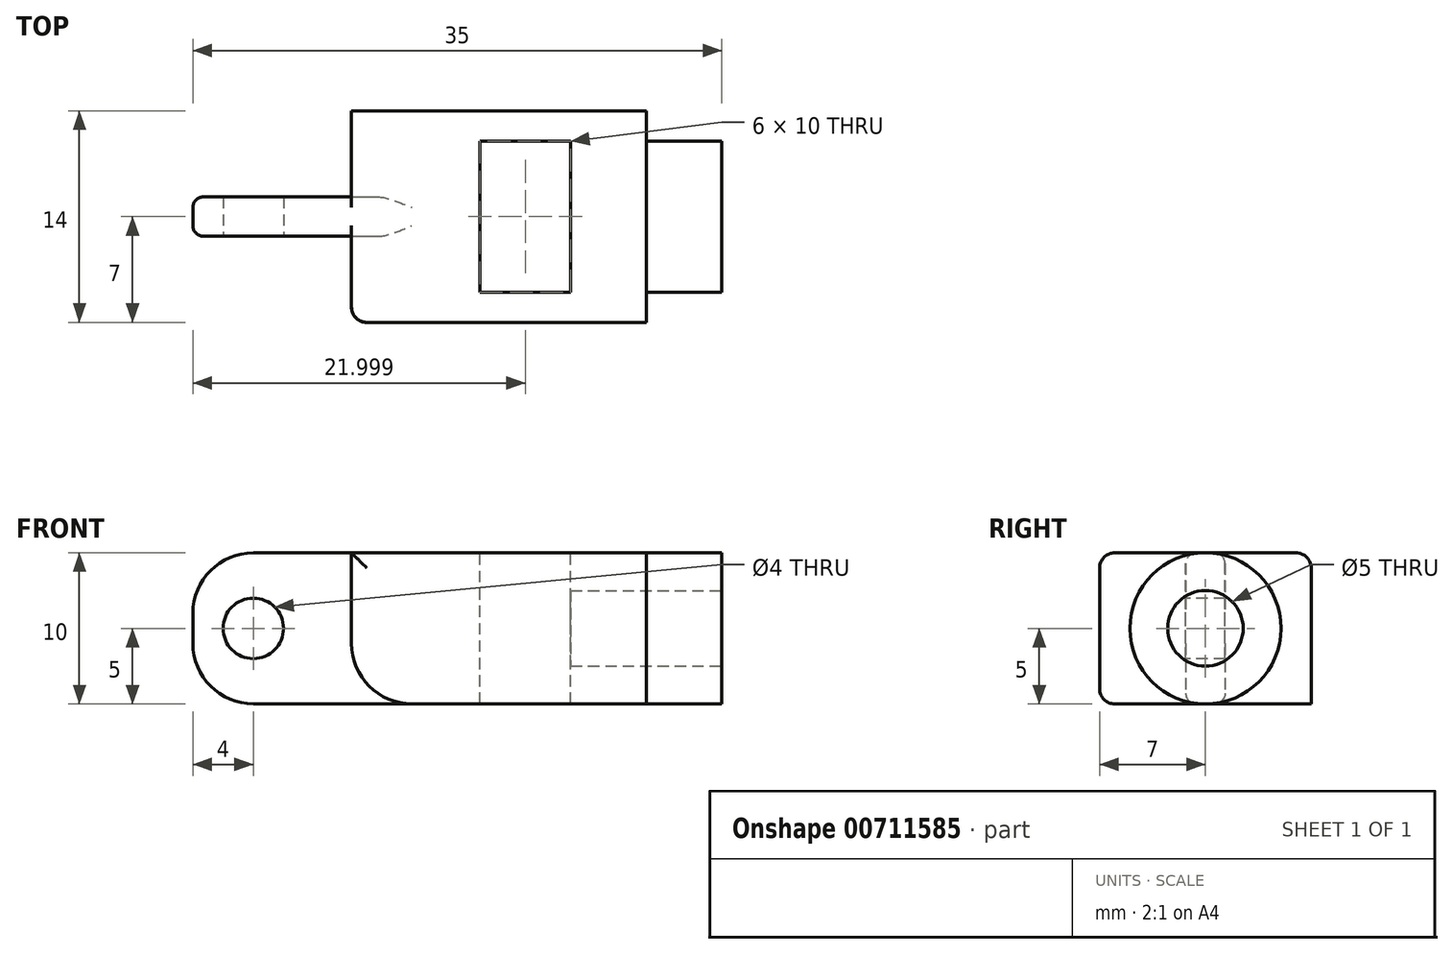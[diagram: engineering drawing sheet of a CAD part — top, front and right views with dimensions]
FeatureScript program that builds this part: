
annotation { "Feature Type Name" : "Feature", "Feature Type Description" : "" }
export const myFeature = defineFeature(function(context is Context, id is Id, definition is map)
    precondition{}
    {
        {
            var Q0;
            Q0=qCreatedBy(makeId("Top.planeOp"),FACE);
            var sketch = newSketch(context, id + "F0", { "sketchPlane" : qUnion([Q0])});
            skLineSegment(sketch, "E0.bottom", {"start": v(-15, 7) * mm, "end": v(15, 7) * mm});
            skLineSegment(sketch, "E0.top", {"start": v(-15, -7) * mm, "end": v(15, -7) * mm});
            skLineSegment(sketch, "E0.left", {"start": v(-15, 7) * mm, "end": v(-15, -7) * mm});
            skLineSegment(sketch, "E0.right", {"start": v(15, 7) * mm, "end": v(15, -7) * mm});
            skLineSegment(sketch, "E1", {"start": v(-15, 0) * mm, "end": v(0, 0) * mm, "construction": true});
            skLineSegment(sketch, "E2", {"start": v(0, 7) * mm, "end": v(0, -0.57) * mm, "construction": true});
            skSolve(sketch);
        }
        {
            var Q0;
            Q0=makeQuery(id+"F0.imprint","IMPRINT",FACE,{"disambiguationData":[TD([[makeQuery(id+"F0.imprint","IMPRINT",EDGE,{"derivedFrom":sQuery(id+"F0.wireOp",EDGE,"E0.bottom")}),-1.0]])]});
            extrude(context, id + "F1", {"entities" : qUnion([Q0]), "depth" : 10 * mm, "offsetDistance" : 25 * mm});
        }
        {
            var Q0;
            Q0=makeQuery(id+"F1.opExtrude","CAP_FACE",FACE,{"disambiguationData":[OSD([sQuery(id+"F0.wireOp",EDGE,"E0.bottom"),sQuery(id+"F0.wireOp",EDGE,"E0.top"),sQuery(id+"F0.wireOp",EDGE,"E0.left"),sQuery(id+"F0.wireOp",EDGE,"E0.right")])],"isStart":false});
            var sketch = newSketch(context, id + "F2", { "sketchPlane" : qUnion([Q0])});
            skLineSegment(sketch, "E3.bottom", {"start": v(-15, -1.3) * mm, "end": v(-4.5, -1.3) * mm});
            skLineSegment(sketch, "E3.top", {"start": v(-15, -7) * mm, "end": v(-4.5, -7) * mm});
            skLineSegment(sketch, "E3.left", {"start": v(-15, -1.3) * mm, "end": v(-15, -7) * mm});
            skLineSegment(sketch, "E3.right", {"start": v(-4.5, -1.3) * mm, "end": v(-4.5, -7) * mm});
            skPoint(sketch, "E4.oppositeSnap0", {"position": v(-4.5, -4.15) * mm});
            skLineSegment(sketch, "E4.bottom", {"start": v(-15, 7) * mm, "end": v(-4.5, 7) * mm});
            skLineSegment(sketch, "E4.top", {"start": v(-15, 1.3) * mm, "end": v(-4.5, 1.3) * mm});
            skLineSegment(sketch, "E4.left", {"start": v(-15, 7) * mm, "end": v(-15, 1.3) * mm});
            skLineSegment(sketch, "E4.right", {"start": v(-4.5, 7) * mm, "end": v(-4.5, 1.3) * mm});
            skSolve(sketch);
        }
        {
            var Q0;
            Q0=makeQuery(id+"F2.imprint","IMPRINT",FACE,{"disambiguationData":[TD([[makeQuery(id+"F2.imprint","IMPRINT",EDGE,{"derivedFrom":sQuery(id+"F2.wireOp",EDGE,"E3.bottom")}),-1.0]])]});
            var Q1;
            Q1=makeQuery(id+"F2.imprint","IMPRINT",FACE,{"disambiguationData":[TD([[makeQuery(id+"F2.imprint","IMPRINT",EDGE,{"derivedFrom":sQuery(id+"F2.wireOp",EDGE,"E4.bottom")}),-1.0]])]});
            extrude(context, id + "F3", {"entities" : qUnion([Q0, Q1]), "operationType" : NewBodyOperationType.REMOVE, "oppositeDirection" : true, "depth" : 25 * mm, "offsetDistance" : 25 * mm});
        }
        {
            var Q0;
            Q0=makeQuery(id+"F1.opExtrude","CAP_EDGE",EDGE,{"disambiguationData":[OSD([sQuery(id+"F0.wireOp",EDGE,"E0.left")])],"isStart":false});
            var Q1;
            Q1=makeQuery(id+"F1.opExtrude","CAP_EDGE",EDGE,{"disambiguationData":[OSD([sQuery(id+"F0.wireOp",EDGE,"E0.left")])],"isStart":true});
            var Q2;
            Q2=makeQuery(id+"F3.boolean.opBoolean","COPY",EDGE,{"derivedFrom":makeQuery(id+"F3.opExtrude","CAP_EDGE",EDGE,{"disambiguationData":[OSD([sQuery(id+"F2.wireOp",EDGE,"E3.right")])],"isStart":true})});
            var Q3;
            Q3=makeQuery(id+"F3.boolean.opBoolean","INTERSECT",EDGE,{"derivedFrom":[makeQuery(id+"F1.opExtrude","CAP_FACE",FACE,{"disambiguationData":[OSD([sQuery(id+"F0.wireOp",EDGE,"E0.bottom"),sQuery(id+"F0.wireOp",EDGE,"E0.top"),sQuery(id+"F0.wireOp",EDGE,"E0.left"),sQuery(id+"F0.wireOp",EDGE,"E0.right")])],"isStart":true}),makeQuery(id+"F3.opExtrude","SWEPT_FACE",FACE,{"disambiguationData":[OSD([sQuery(id+"F2.wireOp",EDGE,"E3.right")])]})]});
            var Q4;
            Q4=makeQuery(id+"F3.boolean.opBoolean","INTERSECT",EDGE,{"derivedFrom":[makeQuery(id+"F1.opExtrude","CAP_FACE",FACE,{"disambiguationData":[OSD([sQuery(id+"F0.wireOp",EDGE,"E0.bottom"),sQuery(id+"F0.wireOp",EDGE,"E0.top"),sQuery(id+"F0.wireOp",EDGE,"E0.left"),sQuery(id+"F0.wireOp",EDGE,"E0.right")])],"isStart":true}),makeQuery(id+"F3.opExtrude","SWEPT_FACE",FACE,{"disambiguationData":[OSD([sQuery(id+"F2.wireOp",EDGE,"E4.right")])]})]});
            var Q5;
            Q5=makeQuery(id+"F3.boolean.opBoolean","COPY",EDGE,{"derivedFrom":makeQuery(id+"F3.opExtrude","CAP_EDGE",EDGE,{"disambiguationData":[OSD([sQuery(id+"F2.wireOp",EDGE,"E4.right")])],"isStart":true})});
            fillet(context, id + "F4", {"entities" : qUnion([Q0, Q1, Q2, Q3, Q4, Q5]), "radius" : 4 * mm, "tangentPropagation" : true, "allowEdgeOverflow" : false});
        }
        {
            var Q0;
            Q0=makeQuery(id+"F3.boolean.opBoolean","COPY",FACE,{"derivedFrom":makeQuery(id+"F3.opExtrude","SWEPT_FACE",FACE,{"disambiguationData":[OSD([sQuery(id+"F2.wireOp",EDGE,"E3.bottom")])]})});
            var sketch = newSketch(context, id + "F5", { "sketchPlane" : qUnion([Q0])});
            skCircle(sketch, "E5", {"center": v(-11, 5) * mm, "radius": 2 * mm});
            skPoint(sketch, "E5.centerSnap0", {"position": v(-15, 5) * mm});
            skSolve(sketch);
        }
        {
            var Q0;
            Q0=makeQuery(id+"F5.imprint","IMPRINT",FACE,{"disambiguationData":[TD([[makeQuery(id+"F5.imprint","IMPRINT",EDGE,{"derivedFrom":sQuery(id+"F5.wireOp",EDGE,"E5")}),1.0]])]});
            extrude(context, id + "F6", {"entities" : qUnion([Q0]), "operationType" : NewBodyOperationType.REMOVE, "oppositeDirection" : true, "depth" : 25 * mm, "offsetDistance" : 25 * mm});
        }
        {
            var Q0;
            Q0=makeQuery(id+"F1.opExtrude","SWEPT_FACE",FACE,{"disambiguationData":[OSD([sQuery(id+"F0.wireOp",EDGE,"E0.right")])]});
            var sketch = newSketch(context, id + "F7", { "sketchPlane" : qUnion([Q0])});
            skPoint(sketch, "E6.oppositeSnap0", {"position": v(7, 5) * mm});
            skPoint(sketch, "E7.centerSnap0", {"position": v(0, 10) * mm});
            skCircle(sketch, "E8", {"center": v(0, 5) * mm, "radius": 5 * mm});
            skSolve(sketch);
        }
        {
            var Q0;
            {var subQ0=sQuery(id+"F7.wireOp",EDGE,"E8");var subQ1=sQuery(id+"F0.wireOp",EDGE,"E0.right");var subQ2=makeQuery(id+"F7.imprint","INTERSECT",VERTEX,{"derivedFrom":[makeQuery(id+"F1.opExtrude","CAP_EDGE",EDGE,{"disambiguationData":[OSD([subQ1])],"isStart":false}),subQ0]});Q0=makeQuery(id+"F7.imprint","IMPRINT",FACE,{"disambiguationData":[TD([[makeQuery(id+"F7.imprint","IMPRINT",EDGE,{"disambiguationData":[TD([[subQ2,1.0]])],"derivedFrom":subQ0}),1.0]])]});}
            extrude(context, id + "F8", {"entities" : qUnion([Q0]), "operationType" : NewBodyOperationType.ADD, "depth" : 5 * mm, "offsetDistance" : 25 * mm});
        }
        {
            var Q0;
            Q0=makeQuery(id+"F1.opExtrude","CAP_FACE",FACE,{"disambiguationData":[OSD([sQuery(id+"F0.wireOp",EDGE,"E0.bottom"),sQuery(id+"F0.wireOp",EDGE,"E0.top"),sQuery(id+"F0.wireOp",EDGE,"E0.left"),sQuery(id+"F0.wireOp",EDGE,"E0.right")])],"isStart":false});
            var sketch = newSketch(context, id + "F9", { "sketchPlane" : qUnion([Q0])});
            skLineSegment(sketch, "E9.bottom", {"start": v(10, 5) * mm, "end": v(4, 5) * mm});
            skLineSegment(sketch, "E9.top", {"start": v(10, -5) * mm, "end": v(4, -5) * mm});
            skLineSegment(sketch, "E9.left", {"start": v(10, 5) * mm, "end": v(10, -5) * mm});
            skLineSegment(sketch, "E9.right", {"start": v(4, 5) * mm, "end": v(4, -5) * mm});
            skSolve(sketch);
        }
        {
            var Q0;
            Q0=makeQuery(id+"F9.imprint","IMPRINT",FACE,{"disambiguationData":[TD([[makeQuery(id+"F9.imprint","IMPRINT",EDGE,{"derivedFrom":sQuery(id+"F9.wireOp",EDGE,"E9.bottom")}),1.0]])]});
            extrude(context, id + "F10", {"entities" : qUnion([Q0]), "operationType" : NewBodyOperationType.REMOVE, "oppositeDirection" : true, "depth" : 12 * mm, "offsetDistance" : 25 * mm});
        }
        {
            var Q0;
            Q0=makeQuery(id+"F3.boolean.opBoolean","COPY",EDGE,{"derivedFrom":makeQuery(id+"F3.opExtrude","CAP_EDGE",EDGE,{"disambiguationData":[OSD([sQuery(id+"F2.wireOp",EDGE,"E3.bottom")])],"isStart":true})});
            var Q1;
            Q1=makeQuery(id+"F3.boolean.opBoolean","INTERSECT",EDGE,{"derivedFrom":[makeQuery(id+"F1.opExtrude","CAP_FACE",FACE,{"disambiguationData":[OSD([sQuery(id+"F0.wireOp",EDGE,"E0.bottom"),sQuery(id+"F0.wireOp",EDGE,"E0.top"),sQuery(id+"F0.wireOp",EDGE,"E0.left"),sQuery(id+"F0.wireOp",EDGE,"E0.right")])],"isStart":true}),makeQuery(id+"F3.opExtrude","SWEPT_FACE",FACE,{"disambiguationData":[OSD([sQuery(id+"F2.wireOp",EDGE,"E3.bottom")])]})]});
            var Q2;
            Q2=makeQuery(id+"F4.opFillet","BLEND_EDGE",EDGE,{"blendedFrom":[makeQuery(id+"F1.opExtrude","CAP_EDGE",EDGE,{"disambiguationData":[OSD([sQuery(id+"F0.wireOp",EDGE,"E0.left")])],"isStart":true}),makeQuery(id+"F3.boolean.opBoolean","COPY",FACE,{"derivedFrom":makeQuery(id+"F3.opExtrude","SWEPT_FACE",FACE,{"disambiguationData":[OSD([sQuery(id+"F2.wireOp",EDGE,"E3.bottom")])]})})],"blendedInto":[makeQuery(id+"F3.boolean.opBoolean","COPY",FACE,{"derivedFrom":makeQuery(id+"F3.opExtrude","SWEPT_FACE",FACE,{"disambiguationData":[OSD([sQuery(id+"F2.wireOp",EDGE,"E3.bottom")])]})})]});
            var Q3;
            Q3=makeQuery(id+"F3.boolean.opBoolean","COPY",EDGE,{"derivedFrom":makeQuery(id+"F3.opExtrude","SWEPT_EDGE",EDGE,{"disambiguationData":[OSD([sQuery(id+"F0.wireOp",EDGE,"E0.left"),sQuery(id+"F2.wireOp",EDGE,"E3.bottom"),sQuery(id+"F2.wireOp",EDGE,"E3.left")])]})});
            var Q4;
            Q4=makeQuery(id+"F4.opFillet","BLEND_EDGE",EDGE,{"blendedFrom":[makeQuery(id+"F1.opExtrude","CAP_EDGE",EDGE,{"disambiguationData":[OSD([sQuery(id+"F0.wireOp",EDGE,"E0.left")])],"isStart":false}),makeQuery(id+"F3.boolean.opBoolean","COPY",FACE,{"derivedFrom":makeQuery(id+"F3.opExtrude","SWEPT_FACE",FACE,{"disambiguationData":[OSD([sQuery(id+"F2.wireOp",EDGE,"E3.bottom")])]})})],"blendedInto":[makeQuery(id+"F3.boolean.opBoolean","COPY",FACE,{"derivedFrom":makeQuery(id+"F3.opExtrude","SWEPT_FACE",FACE,{"disambiguationData":[OSD([sQuery(id+"F2.wireOp",EDGE,"E3.bottom")])]})})]});
            var Q5;
            Q5=makeQuery(id+"F3.boolean.opBoolean","INTERSECT",EDGE,{"derivedFrom":[makeQuery(id+"F1.opExtrude","CAP_FACE",FACE,{"disambiguationData":[OSD([sQuery(id+"F0.wireOp",EDGE,"E0.bottom"),sQuery(id+"F0.wireOp",EDGE,"E0.top"),sQuery(id+"F0.wireOp",EDGE,"E0.left"),sQuery(id+"F0.wireOp",EDGE,"E0.right")])],"isStart":true}),makeQuery(id+"F3.opExtrude","SWEPT_FACE",FACE,{"disambiguationData":[OSD([sQuery(id+"F2.wireOp",EDGE,"E4.top")])]})]});
            var Q6;
            Q6=makeQuery(id+"F4.opFillet","BLEND_EDGE",EDGE,{"blendedFrom":[makeQuery(id+"F1.opExtrude","CAP_EDGE",EDGE,{"disambiguationData":[OSD([sQuery(id+"F0.wireOp",EDGE,"E0.left")])],"isStart":true}),makeQuery(id+"F3.boolean.opBoolean","COPY",FACE,{"derivedFrom":makeQuery(id+"F3.opExtrude","SWEPT_FACE",FACE,{"disambiguationData":[OSD([sQuery(id+"F2.wireOp",EDGE,"E4.top")])]})})],"blendedInto":[makeQuery(id+"F3.boolean.opBoolean","COPY",FACE,{"derivedFrom":makeQuery(id+"F3.opExtrude","SWEPT_FACE",FACE,{"disambiguationData":[OSD([sQuery(id+"F2.wireOp",EDGE,"E4.top")])]})})]});
            var Q7;
            Q7=makeQuery(id+"F3.boolean.opBoolean","COPY",EDGE,{"derivedFrom":makeQuery(id+"F3.opExtrude","SWEPT_EDGE",EDGE,{"disambiguationData":[OSD([sQuery(id+"F0.wireOp",EDGE,"E0.left"),sQuery(id+"F2.wireOp",EDGE,"E4.top"),sQuery(id+"F2.wireOp",EDGE,"E4.left")])]})});
            var Q8;
            Q8=makeQuery(id+"F4.opFillet","BLEND_EDGE",EDGE,{"blendedFrom":[makeQuery(id+"F1.opExtrude","CAP_EDGE",EDGE,{"disambiguationData":[OSD([sQuery(id+"F0.wireOp",EDGE,"E0.left")])],"isStart":false}),makeQuery(id+"F3.boolean.opBoolean","COPY",FACE,{"derivedFrom":makeQuery(id+"F3.opExtrude","SWEPT_FACE",FACE,{"disambiguationData":[OSD([sQuery(id+"F2.wireOp",EDGE,"E4.top")])]})})],"blendedInto":[makeQuery(id+"F3.boolean.opBoolean","COPY",FACE,{"derivedFrom":makeQuery(id+"F3.opExtrude","SWEPT_FACE",FACE,{"disambiguationData":[OSD([sQuery(id+"F2.wireOp",EDGE,"E4.top")])]})})]});
            var Q9;
            Q9=makeQuery(id+"F3.boolean.opBoolean","COPY",EDGE,{"derivedFrom":makeQuery(id+"F3.opExtrude","CAP_EDGE",EDGE,{"disambiguationData":[OSD([sQuery(id+"F2.wireOp",EDGE,"E4.top")])],"isStart":true})});
            fillet(context, id + "F11", {"entities" : qUnion([Q0, Q1, Q2, Q3, Q4, Q5, Q6, Q7, Q8, Q9]), "radius" : 0.7 * mm, "tangentPropagation" : true, "allowEdgeOverflow" : false});
        }
        {
            var Q0;
            Q0=makeQuery(id+"F1.opExtrude","CAP_EDGE",EDGE,{"disambiguationData":[OSD([sQuery(id+"F0.wireOp",EDGE,"E0.top")])],"isStart":false});
            var Q1;
            {var subQ0=sQuery(id+"F0.wireOp",EDGE,"E0.top");Q1=makeQuery(id+"F4.opFillet","BLEND_EDGE",EDGE,{"blendedFrom":[makeQuery(id+"F3.boolean.opBoolean","INTERSECT",EDGE,{"derivedFrom":[makeQuery(id+"F1.opExtrude","CAP_FACE",FACE,{"disambiguationData":[OSD([sQuery(id+"F0.wireOp",EDGE,"E0.bottom"),subQ0,sQuery(id+"F0.wireOp",EDGE,"E0.left"),sQuery(id+"F0.wireOp",EDGE,"E0.right")])],"isStart":true}),makeQuery(id+"F3.opExtrude","SWEPT_FACE",FACE,{"disambiguationData":[OSD([sQuery(id+"F2.wireOp",EDGE,"E3.right")])]})]}),makeQuery(id+"F1.opExtrude","SWEPT_FACE",FACE,{"disambiguationData":[OSD([subQ0])]})],"blendedInto":[makeQuery(id+"F1.opExtrude","SWEPT_FACE",FACE,{"disambiguationData":[OSD([subQ0])]})]});}
            var Q2;
            Q2=makeQuery(id+"F3.boolean.opBoolean","COPY",EDGE,{"derivedFrom":makeQuery(id+"F3.opExtrude","SWEPT_EDGE",EDGE,{"disambiguationData":[OSD([sQuery(id+"F0.wireOp",EDGE,"E0.top"),sQuery(id+"F2.wireOp",EDGE,"E3.top"),sQuery(id+"F2.wireOp",EDGE,"E3.right")])]})});
            var Q3;
            Q3=makeQuery(id+"F4.opFillet","BLEND_EDGE",EDGE,{"blendedFrom":[makeQuery(id+"F3.boolean.opBoolean","COPY",EDGE,{"derivedFrom":makeQuery(id+"F3.opExtrude","CAP_EDGE",EDGE,{"disambiguationData":[OSD([sQuery(id+"F2.wireOp",EDGE,"E3.right")])],"isStart":true})}),makeQuery(id+"F1.opExtrude","SWEPT_FACE",FACE,{"disambiguationData":[OSD([sQuery(id+"F0.wireOp",EDGE,"E0.top")])]})],"blendedInto":[makeQuery(id+"F1.opExtrude","SWEPT_FACE",FACE,{"disambiguationData":[OSD([sQuery(id+"F0.wireOp",EDGE,"E0.top")])]})]});
            var Q4;
            Q4=makeQuery(id+"F1.opExtrude","CAP_EDGE",EDGE,{"disambiguationData":[OSD([sQuery(id+"F0.wireOp",EDGE,"E0.bottom")])],"isStart":false});
            fillet(context, id + "F12", {"entities" : qUnion([Q0, Q1, Q2, Q3, Q4]), "radius" : 1 * mm, "tangentPropagation" : true, "allowEdgeOverflow" : false});
        }
        {
            var Q0;
            Q0=makeQuery(id+"F8.opExtrude","CAP_FACE",FACE,{"disambiguationData":[OSD([sQuery(id+"F7.wireOp",EDGE,"E8")])],"isStart":false});
            var sketch = newSketch(context, id + "F13", { "sketchPlane" : qUnion([Q0])});
            skCircle(sketch, "E10", {"center": v(0, 5) * mm, "radius": 2.5 * mm});
            skSolve(sketch);
        }
        {
            var Q0;
            Q0=makeQuery(id+"F13.imprint","IMPRINT",FACE,{"disambiguationData":[TD([[makeQuery(id+"F13.imprint","IMPRINT",EDGE,{"derivedFrom":sQuery(id+"F13.wireOp",EDGE,"E10")}),1.0]])]});
            extrude(context, id + "F14", {"entities" : qUnion([Q0]), "operationType" : NewBodyOperationType.REMOVE, "oppositeDirection" : true, "depth" : 15 * mm, "offsetDistance" : 25 * mm});
        }
    });
